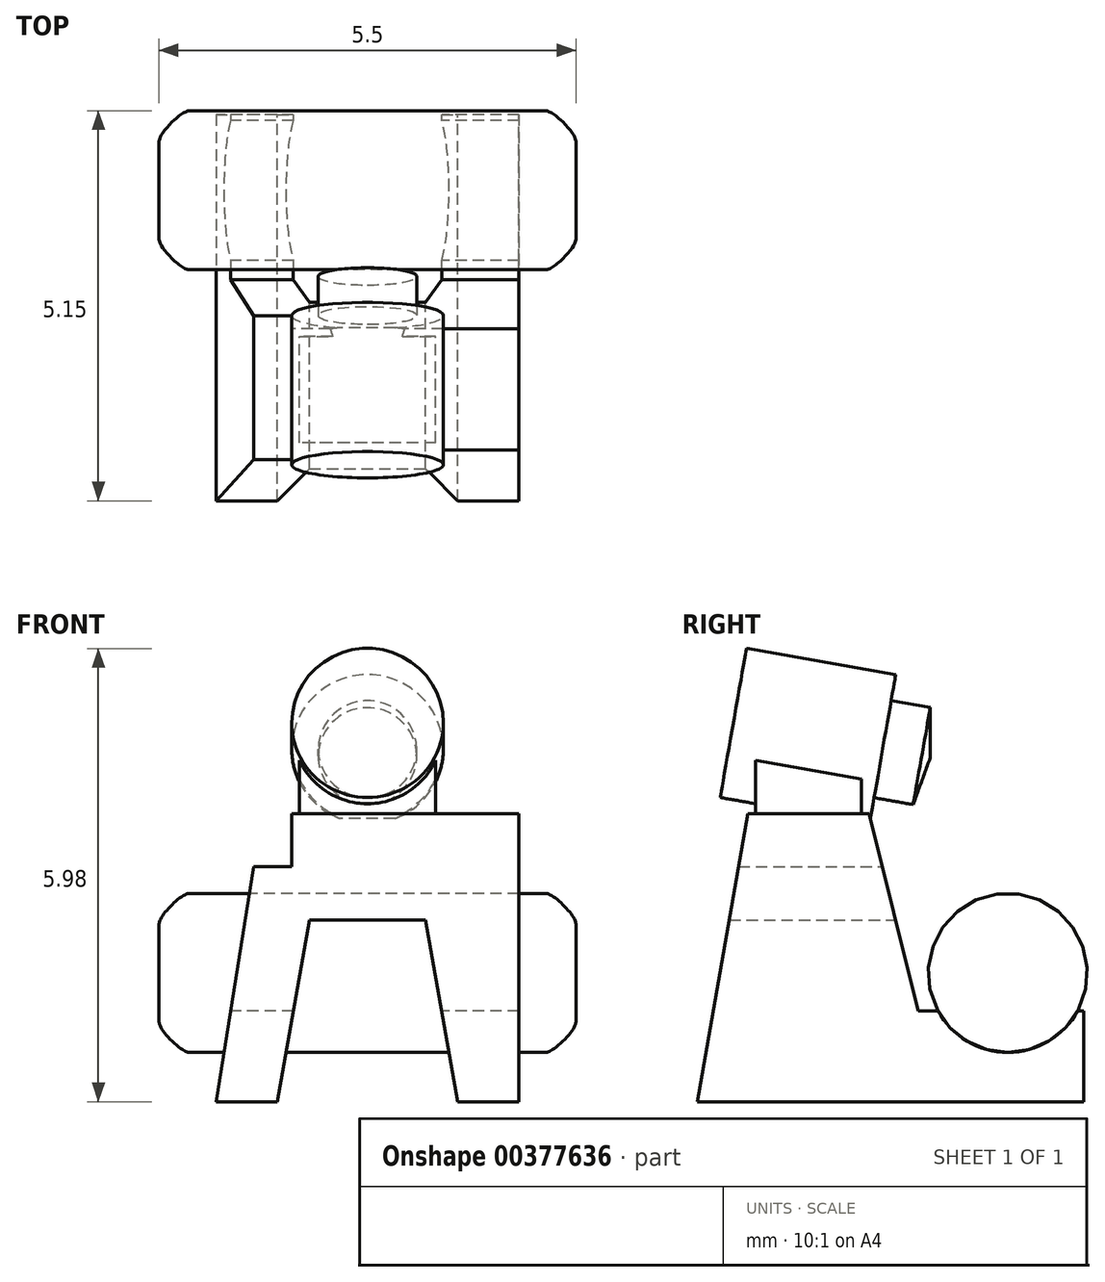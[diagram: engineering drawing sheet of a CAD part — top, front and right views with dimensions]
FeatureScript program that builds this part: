
annotation { "Feature Type Name" : "Feature", "Feature Type Description" : "" }
export const myFeature = defineFeature(function(context is Context, id is Id, definition is map)
    precondition{}
    {
        {
            var Q0;
            Q0=qCreatedBy(makeId("Right.planeOp"),FACE);
            var sketch = newSketch(context, id + "F0", { "sketchPlane" : qUnion([Q0])});
            skLineSegment(sketch, "E0", {"start": v(0.67, 3.8) * mm, "end": v(0, 0) * mm});
            skLineSegment(sketch, "E1", {"start": v(0.67, 3.8) * mm, "end": v(2.27, 3.8) * mm});
            skLineSegment(sketch, "E2", {"start": v(2.27, 3.8) * mm, "end": v(2.92, 1.2) * mm});
            skLineSegment(sketch, "E3", {"start": v(2.92, 1.2) * mm, "end": v(5.1, 1.2) * mm});
            skLineSegment(sketch, "E4", {"start": v(5.1, 1.2) * mm, "end": v(5.1, 0) * mm});
            skLineSegment(sketch, "E5", {"start": v(5.1, 0) * mm, "end": v(0, 0) * mm});
            skSolve(sketch);
        }
        {
            var Q0;
            Q0=qSketchRegion(id+"F0",true);
            extrude(context, id + "F1", {"entities" : qUnion([Q0]), "depth" : 2 * mm, "hasSecondDirection" : true, "secondDirectionOppositeDirection" : true, "secondDirectionDepth" : 2 * mm});
        }
        {
            var Q0;
            Q0=makeQuery(id+"F1.opExtrude","SWEPT_FACE",FACE,{"disambiguationData":[OSD([sQuery(id+"F0.wireOp",EDGE,"E4")])]});
            var sketch = newSketch(context, id + "F2", { "sketchPlane" : qUnion([Q0])});
            skLineSegment(sketch, "E6.0", {"start": v(1, 3.8) * mm, "end": v(2, 3.8) * mm});
            skLineSegment(sketch, "E7", {"start": v(2, 3.8) * mm, "end": v(2, 0) * mm});
            skLineSegment(sketch, "E8", {"start": v(2, 0) * mm, "end": v(1.5, 3.1) * mm});
            skLineSegment(sketch, "E9", {"start": v(1.5, 3.1) * mm, "end": v(1, 3.1) * mm});
            skLineSegment(sketch, "E10", {"start": v(1, 3.1) * mm, "end": v(1, 3.8) * mm});
            skPoint(sketch, "E11.orphan", {"position": v(-2, 3.8) * mm});
            skSolve(sketch);
        }
        {
            var Q0;
            Q0=qSketchRegion(id+"F2",true);
            var Q1;
            Q1=makeQuery(id+"F1.opExtrude","SWEPT_FACE",FACE,{"disambiguationData":[OSD([sQuery(id+"F0.wireOp",EDGE,"E0")])]});
            extrude(context, id + "F3", {"entities" : qUnion([Q0]), "operationType" : NewBodyOperationType.REMOVE, "endBound" : BoundingType.UP_TO_SURFACE, "oppositeDirection" : true, "endBoundEntityFace" : qUnion([Q1]), "depth" : 25 * mm});
        }
        {
            var Q0;
            Q0=makeQuery(id+"F1.opExtrude","SWEPT_FACE",FACE,{"disambiguationData":[OSD([sQuery(id+"F0.wireOp",EDGE,"E4")])]});
            var sketch = newSketch(context, id + "F4", { "sketchPlane" : qUnion([Q0])});
            skLineSegment(sketch, "E12", {"start": v(1.19, 0) * mm, "end": v(0.77, 2.4) * mm});
            skLineSegment(sketch, "E13", {"start": v(0.77, 2.4) * mm, "end": v(-0.77, 2.4) * mm});
            skLineSegment(sketch, "E14", {"start": v(-0.77, 2.4) * mm, "end": v(-1.19, 0) * mm});
            skLineSegment(sketch, "E15", {"start": v(-1.19, 0) * mm, "end": v(1.19, 0) * mm});
            skLineSegment(sketch, "E16", {"start": v(0, 0) * mm, "end": v(0, 2.4) * mm, "construction": true});
            skSolve(sketch);
        }
        {
            var Q0;
            Q0=qSketchRegion(id+"F4",true);
            extrude(context, id + "F5", {"entities" : qUnion([Q0]), "operationType" : NewBodyOperationType.REMOVE, "endBound" : BoundingType.THROUGH_ALL, "oppositeDirection" : true, "depth" : 25 * mm});
        }
        {
            var Q0;
            Q0=qCreatedBy(makeId("Right.planeOp"),FACE);
            var sketch = newSketch(context, id + "F6", { "sketchPlane" : qUnion([Q0])});
            skLineSegment(sketch, "E17", {"start": v(0.48, 5) * mm, "end": v(3.78, 4.42) * mm, "construction": true});
            skLineSegment(sketch, "E18", {"start": v(0.48, 5) * mm, "end": v(0.65, 5.98) * mm});
            skLineSegment(sketch, "E19", {"start": v(0.65, 5.98) * mm, "end": v(2.62, 5.64) * mm});
            skLineSegment(sketch, "E20", {"start": v(2.62, 5.64) * mm, "end": v(2.56, 5.3) * mm});
            skLineSegment(sketch, "E21", {"start": v(2.56, 5.3) * mm, "end": v(3.08, 5.2) * mm});
            skLineSegment(sketch, "E22", {"start": v(3.08, 5.2) * mm, "end": v(3.08, 4.54) * mm});
            skLineSegment(sketch, "E23", {"start": v(3.08, 4.54) * mm, "end": v(0.48, 5) * mm});
            skSolve(sketch);
        }
        {
            var Q0;
            Q0=makeQuery(id+"F6.imprint","IMPRINT",FACE,{"disambiguationData":[TD([[makeQuery(id+"F6.imprint","IMPRINT",EDGE,{"derivedFrom":sQuery(id+"F6.wireOp",EDGE,"E18")}),-1.0]])]});
            var Q1;
            Q1=sQuery(id+"F6.wireOp",EDGE,"E17");
            revolve(context, id + "F7", {"entities" : qUnion([Q0]), "axis" : qUnion([Q1]), "revolveType" : RevolveType.FULL});
        }
        {
            var Q0;
            Q0=qCreatedBy(makeId("Right.planeOp"),FACE);
            var sketch = newSketch(context, id + "F8", { "sketchPlane" : qUnion([Q0])});
            skLineSegment(sketch, "E24", {"start": v(0.77, 3.8) * mm, "end": v(2.17, 3.8) * mm});
            skLineSegment(sketch, "E25", {"start": v(2.17, 3.8) * mm, "end": v(2.17, 5) * mm});
            skLineSegment(sketch, "E26", {"start": v(2.17, 5) * mm, "end": v(0.77, 5) * mm});
            skLineSegment(sketch, "E27", {"start": v(0.77, 5) * mm, "end": v(0.77, 3.8) * mm});
            skSolve(sketch);
        }
        {
            var Q0;
            Q0=qSketchRegion(id+"F8",true);
            extrude(context, id + "F9", {"entities" : qUnion([Q0]), "operationType" : NewBodyOperationType.ADD, "depth" : 0.9 * mm, "hasSecondDirection" : true, "secondDirectionOppositeDirection" : true, "secondDirectionDepth" : 0.9 * mm});
        }
        {
            var Q0;
            Q0=qCreatedBy(makeId("Right.planeOp"),FACE);
            var sketch = newSketch(context, id + "F10", { "sketchPlane" : qUnion([Q0])});
            skCircle(sketch, "E28", {"center": v(4.1, 1.7) * mm, "radius": 1.05 * mm});
            skSolve(sketch);
        }
        {
            var Q0;
            Q0=qSketchRegion(id+"F10",true);
            extrude(context, id + "F11", {"entities" : qUnion([Q0]), "operationType" : NewBodyOperationType.ADD, "endBound" : BoundingType.SYMMETRIC, "depth" : 5.5 * mm});
        }
        {
            var Q0;
            Q0=makeQuery(id+"F11.opExtrude","CAP_EDGE",EDGE,{"disambiguationData":[OSD([sQuery(id+"F10.wireOp",EDGE,"E28")])],"isStart":false});
            var Q1;
            Q1=makeQuery(id+"F11.opExtrude","CAP_EDGE",EDGE,{"disambiguationData":[OSD([sQuery(id+"F10.wireOp",EDGE,"E28")])],"isStart":true});
            fillet(context, id + "F12", {"entities" : qUnion([Q0, Q1]), "radius" : 0.4 * mm, "tangentPropagation" : true, "rho" : 0.2, "crossSection" : FilletCrossSection.CONIC, "allowEdgeOverflow" : false});
        }
    });
